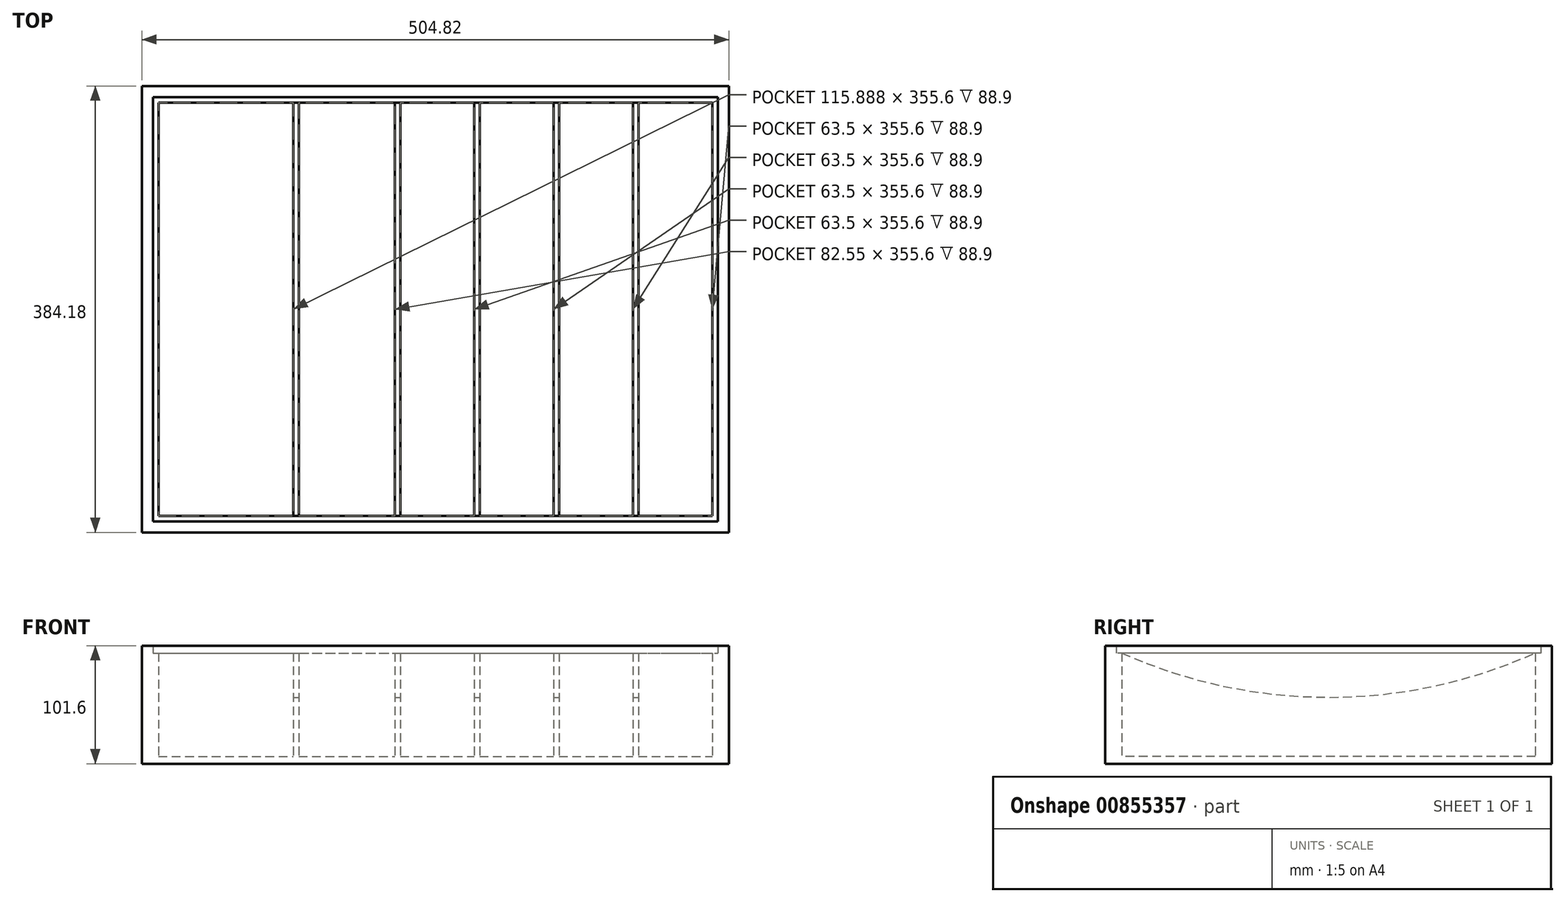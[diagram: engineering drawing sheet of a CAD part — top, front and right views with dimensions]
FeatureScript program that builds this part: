
annotation { "Feature Type Name" : "Feature", "Feature Type Description" : "" }
export const myFeature = defineFeature(function(context is Context, id is Id, definition is map)
    precondition{}
    {
        {
            var Q0;
            Q0=qCreatedBy(makeId("Top.planeOp"),FACE);
            var sketch = newSketch(context, id + "F0", { "sketchPlane" : qUnion([Q0])});
            skLineSegment(sketch, "E0.bottom", {"start": v(-144.1, 266.85) * mm, "end": v(360.73, 266.85) * mm});
            skLineSegment(sketch, "E0.top", {"start": v(-144.1, -117.33) * mm, "end": v(360.73, -117.33) * mm});
            skLineSegment(sketch, "E0.left", {"start": v(-144.1, 266.85) * mm, "end": v(-144.1, -117.33) * mm});
            skLineSegment(sketch, "E0.right", {"start": v(360.73, 266.85) * mm, "end": v(360.73, -117.33) * mm});
            skLineSegment(sketch, "E1.0", {"start": v(-134.57, 257.32) * mm, "end": v(-134.57, -107.8) * mm});
            skLineSegment(sketch, "E1.1", {"start": v(-134.57, 257.32) * mm, "end": v(351.2, 257.32) * mm});
            skLineSegment(sketch, "E1.2", {"start": v(351.2, 257.32) * mm, "end": v(351.2, -107.8) * mm});
            skLineSegment(sketch, "E1.3", {"start": v(-134.57, -107.8) * mm, "end": v(351.2, -107.8) * mm});
            skLineSegment(sketch, "E2.0", {"start": v(-129.8, 252.56) * mm, "end": v(-13.92, 252.56) * mm});
            skLineSegment(sketch, "E2.1", {"start": v(-129.8, 252.56) * mm, "end": v(-129.8, -103.04) * mm});
            skLineSegment(sketch, "E2.2", {"start": v(-129.8, -103.04) * mm, "end": v(-13.92, -103.04) * mm});
            skLineSegment(sketch, "E2.3", {"start": v(346.45, 252.56) * mm, "end": v(346.45, -103.04) * mm});
            skLineSegment(sketch, "E3", {"start": v(-9.15, 252.56) * mm, "end": v(-9.15, -103.04) * mm});
            skLineSegment(sketch, "E4", {"start": v(78.16, 252.56) * mm, "end": v(78.16, -103.04) * mm});
            skLineSegment(sketch, "E5", {"start": v(146.42, 252.56) * mm, "end": v(146.42, -103.04) * mm});
            skLineSegment(sketch, "E6", {"start": v(214.68, 252.56) * mm, "end": v(214.68, -103.04) * mm});
            skLineSegment(sketch, "E7", {"start": v(282.95, 252.56) * mm, "end": v(282.95, -103.04) * mm});
            skLineSegment(sketch, "E8.0", {"start": v(-13.92, 252.56) * mm, "end": v(-13.92, -103.04) * mm});
            skLineSegment(sketch, "E9.0", {"start": v(73.4, 252.56) * mm, "end": v(73.4, -103.04) * mm});
            skLineSegment(sketch, "E10.0", {"start": v(141.66, 252.56) * mm, "end": v(141.66, -103.04) * mm});
            skLineSegment(sketch, "E11.0", {"start": v(209.92, 252.56) * mm, "end": v(209.92, -103.04) * mm});
            skLineSegment(sketch, "E12.0", {"start": v(278.18, 252.56) * mm, "end": v(278.18, -103.04) * mm});
            skLineSegment(sketch, "E13.trimOffspring", {"start": v(-9.15, 252.56) * mm, "end": v(73.4, 252.56) * mm});
            skLineSegment(sketch, "E14.trimOffspring", {"start": v(78.16, 252.56) * mm, "end": v(141.66, 252.56) * mm});
            skLineSegment(sketch, "E15.trimOffspring", {"start": v(146.42, 252.56) * mm, "end": v(209.92, 252.56) * mm});
            skLineSegment(sketch, "E16.trimOffspring", {"start": v(214.68, 252.56) * mm, "end": v(278.18, 252.56) * mm});
            skLineSegment(sketch, "E17.trimOffspring", {"start": v(282.95, 252.56) * mm, "end": v(346.45, 252.56) * mm});
            skLineSegment(sketch, "E18.trimOffspring", {"start": v(282.95, -103.04) * mm, "end": v(346.45, -103.04) * mm});
            skLineSegment(sketch, "E19.trimOffspring", {"start": v(214.68, -103.04) * mm, "end": v(278.18, -103.04) * mm});
            skLineSegment(sketch, "E20.trimOffspring", {"start": v(146.42, -103.04) * mm, "end": v(209.92, -103.04) * mm});
            skLineSegment(sketch, "E21.trimOffspring", {"start": v(78.16, -103.04) * mm, "end": v(141.66, -103.04) * mm});
            skLineSegment(sketch, "E22.trimOffspring", {"start": v(-9.15, -103.04) * mm, "end": v(73.4, -103.04) * mm});
            skSolve(sketch);
        }
        {
            var Q0;
            Q0=makeQuery(id+"F0.imprint","IMPRINT",FACE,{"disambiguationData":[TD([[makeQuery(id+"F0.imprint","IMPRINT",EDGE,{"derivedFrom":sQuery(id+"F0.wireOp",EDGE,"E0.bottom")}),-1.0]])]});
            extrude(context, id + "F1", {"entities" : qUnion([Q0]), "depth" : 95.25 * mm, "offsetDistance" : 25.4 * mm});
        }
        {
            var Q0;
            Q0=makeQuery(id+"F0.imprint","IMPRINT",FACE,{"disambiguationData":[TD([[makeQuery(id+"F0.imprint","IMPRINT",EDGE,{"derivedFrom":sQuery(id+"F0.wireOp",EDGE,"E1.0")}),1.0]])]});
            extrude(context, id + "F2", {"entities" : qUnion([Q0]), "depth" : 88.9 * mm, "offsetDistance" : 25.4 * mm});
        }
        {
            var Q0;
            Q0=makeQuery(id+"F0.imprint","IMPRINT",FACE,{"disambiguationData":[TD([[makeQuery(id+"F0.imprint","IMPRINT",EDGE,{"derivedFrom":sQuery(id+"F0.wireOp",EDGE,"E0.bottom")}),-1.0]])]});
            var sketch = newSketch(context, id + "F3", { "sketchPlane" : qUnion([Q0])});
            skLineSegment(sketch, "E23.0", {"start": v(-144.1, -117.33) * mm, "end": v(360.73, -117.33) * mm});
            skLineSegment(sketch, "E24.0", {"start": v(360.73, 266.85) * mm, "end": v(360.73, -117.33) * mm});
            skLineSegment(sketch, "E25.0", {"start": v(-144.1, 266.85) * mm, "end": v(360.73, 266.85) * mm});
            skLineSegment(sketch, "E26.0", {"start": v(-144.1, 266.85) * mm, "end": v(-144.1, -117.33) * mm});
            skLineSegment(sketch, "E27.left", {"start": v(-144.1, -117.33) * mm, "end": v(-144.1, 266.85) * mm});
            skLineSegment(sketch, "E27.right", {"start": v(360.73, -117.33) * mm, "end": v(360.73, 266.85) * mm});
            skSolve(sketch);
        }
        {
            var Q0;
            Q0 = qSketchRegion(id + "F3", true);
            extrude(context, id + "F4", {"entities" : qUnion([Q0]), "operationType" : NewBodyOperationType.ADD, "oppositeDirection" : true, "depth" : 6.35 * mm, "offsetDistance" : 25.4 * mm});
        }
        {
            var Q0;
            Q0=makeQuery(id+"F2.opExtrude","SWEPT_FACE",FACE,{"disambiguationData":[OSD([sQuery(id+"F0.wireOp",EDGE,"E7")])]});
            var sketch = newSketch(context, id + "F5", { "sketchPlane" : qUnion([Q0])});
            skLineSegment(sketch, "E28", {"start": v(74.76, 88.9) * mm, "end": v(74.76, 50.8) * mm, "construction": true});
            skArc(sketch, "E29", {"start": v(-103.04, 88.9) * mm, "mid": v(74.76, 50.8) * mm, "end": v(252.56, 88.9) * mm});
            skLineSegment(sketch, "E30", {"start": v(-103.04, 88.9) * mm, "end": v(252.56, 88.9) * mm});
            skSolve(sketch);
        }
        {
            var Q0;
            Q0=makeQuery(id+"F5.imprint","IMPRINT",FACE,{"disambiguationData":[TD([[makeQuery(id+"F5.imprint","IMPRINT",EDGE,{"derivedFrom":sQuery(id+"F5.wireOp",EDGE,"E29")}),1.0]])]});
            var Q1;
            Q1=makeQuery(id+"F2.opExtrude","SWEPT_FACE",FACE,{"disambiguationData":[OSD([sQuery(id+"F0.wireOp",EDGE,"E8.0")])]});
            extrude(context, id + "F6", {"entities" : qUnion([Q0]), "operationType" : NewBodyOperationType.REMOVE, "endBound" : BoundingType.UP_TO_SURFACE, "oppositeDirection" : true, "depth" : 25.4 * mm, "endBoundEntityFace" : qUnion([Q1]), "offsetDistance" : 25.4 * mm});
        }
    });
